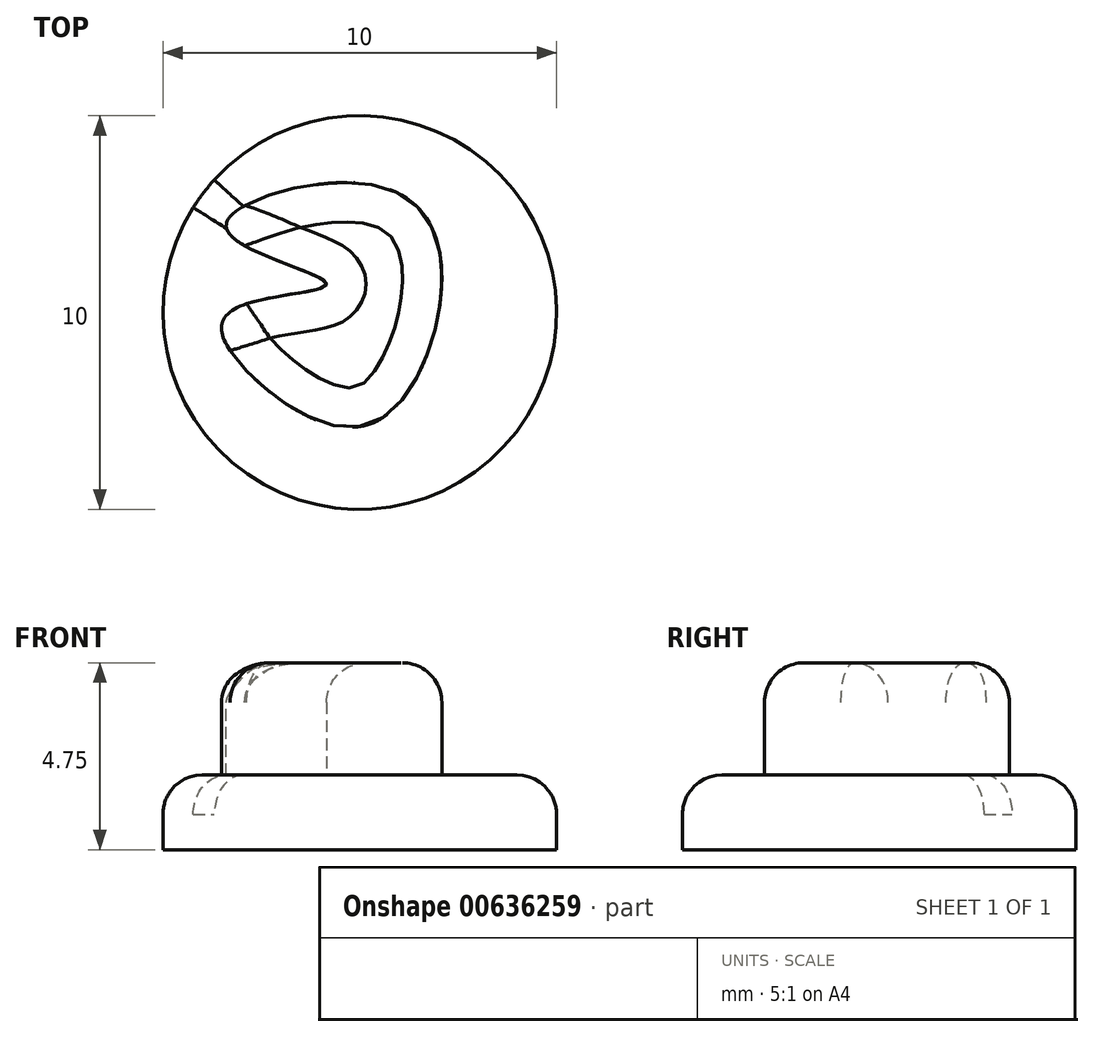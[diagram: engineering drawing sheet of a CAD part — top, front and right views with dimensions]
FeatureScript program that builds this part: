
annotation { "Feature Type Name" : "Feature", "Feature Type Description" : "" }
export const myFeature = defineFeature(function(context is Context, id is Id, definition is map)
    precondition{}
    {
        {
            var Q0;
            Q0=qCreatedBy(makeId("Top.planeOp"),FACE);
            var sketch = newSketch(context, id + "F0", { "sketchPlane" : qUnion([Q0])});
            skCircle(sketch, "E0", {"center": v(0, 0) * mm, "radius": 5 * mm});
            skSolve(sketch);
        }
        {
            var Q0;
            Q0=makeQuery(id+"F0.imprint","IMPRINT",FACE,{"disambiguationData":[TD([[makeQuery(id+"F0.imprint","IMPRINT",EDGE,{"derivedFrom":sQuery(id+"F0.wireOp",EDGE,"E0")}),1.0]])]});
            extrude(context, id + "F1", {"entities" : qUnion([Q0]), "depth" : 1.9 * mm, "offsetDistance" : 25 * mm});
        }
        {
            var Q0;
            Q0=makeQuery(id+"F1.opExtrude","CAP_FACE",FACE,{"disambiguationData":[OSD([sQuery(id+"F0.wireOp",EDGE,"E0")])],"isStart":false});
            var sketch = newSketch(context, id + "F2", { "sketchPlane" : qUnion([Q0])});
            skFitSpline(sketch, "E1", {"points": [v(-3.37, 2.09) * mm, v(0, 3.29) * mm, v(2.07, 1.26) * mm, v(0.45, -2.75) * mm, v(-2.54, -1.8) * mm, v(-3.32, 0) * mm, v(-0.84, 0.73) * mm, v(-3.37, 2.09) * mm]});
            skSolve(sketch);
        }
        {
            var Q0;
            Q0=makeQuery(id+"F2.imprint","IMPRINT",FACE,{"disambiguationData":[TD([[makeQuery(id+"F2.imprint","IMPRINT",EDGE,{"derivedFrom":sQuery(id+"F2.wireOp",EDGE,"E1")}),-1.0]])]});
            extrude(context, id + "F3", {"entities" : qUnion([Q0]), "operationType" : NewBodyOperationType.ADD, "depth" : 2.85 * mm, "offsetDistance" : 25 * mm});
        }
        {
            var Q0;
            Q0=makeQuery(id+"F3.opExtrude","CAP_EDGE",EDGE,{"disambiguationData":[OSD([sQuery(id+"F2.wireOp",EDGE,"E1")])],"isStart":false});
            fillet(context, id + "F4", {"entities" : qUnion([Q0]), "radius" : 1 * mm, "tangentPropagation" : true, "allowEdgeOverflow" : false});
        }
        {
            var Q0;
            Q0=makeQuery(id+"F1.opExtrude","CAP_EDGE",EDGE,{"disambiguationData":[OSD([sQuery(id+"F0.wireOp",EDGE,"E0")])],"isStart":false});
            fillet(context, id + "F5", {"entities" : qUnion([Q0]), "radius" : 1 * mm, "tangentPropagation" : true, "allowEdgeOverflow" : false});
        }
    });
